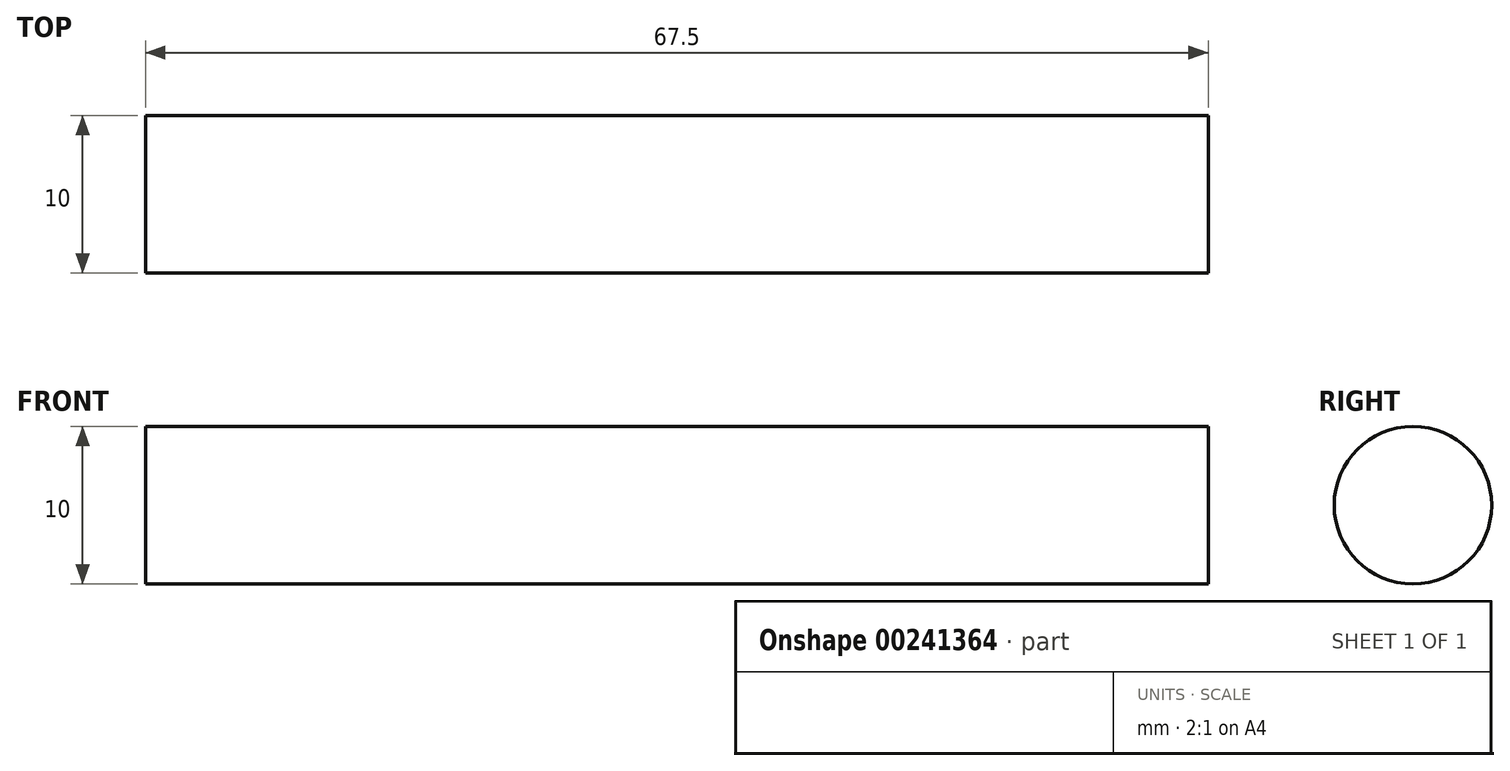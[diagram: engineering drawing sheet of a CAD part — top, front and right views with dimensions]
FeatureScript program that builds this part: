
annotation { "Feature Type Name" : "Feature", "Feature Type Description" : "" }
export const myFeature = defineFeature(function(context is Context, id is Id, definition is map)
    precondition{}
    {
        {
            var Q0;
            Q0=qCreatedBy(makeId("Right.planeOp"),FACE);
            var sketch = newSketch(context, id + "F0", { "sketchPlane" : qUnion([Q0])});
            skCircle(sketch, "E0", {"center": v(0, 0) * mm, "radius": 5 * mm});
            skSolve(sketch);
        }
        {
            var Q0;
            Q0 = qSketchRegion(id + "F0", true);
            extrude(context, id + "F1", {"entities" : qUnion([Q0]), "depth" : 67.5 * mm});
        }
    });
